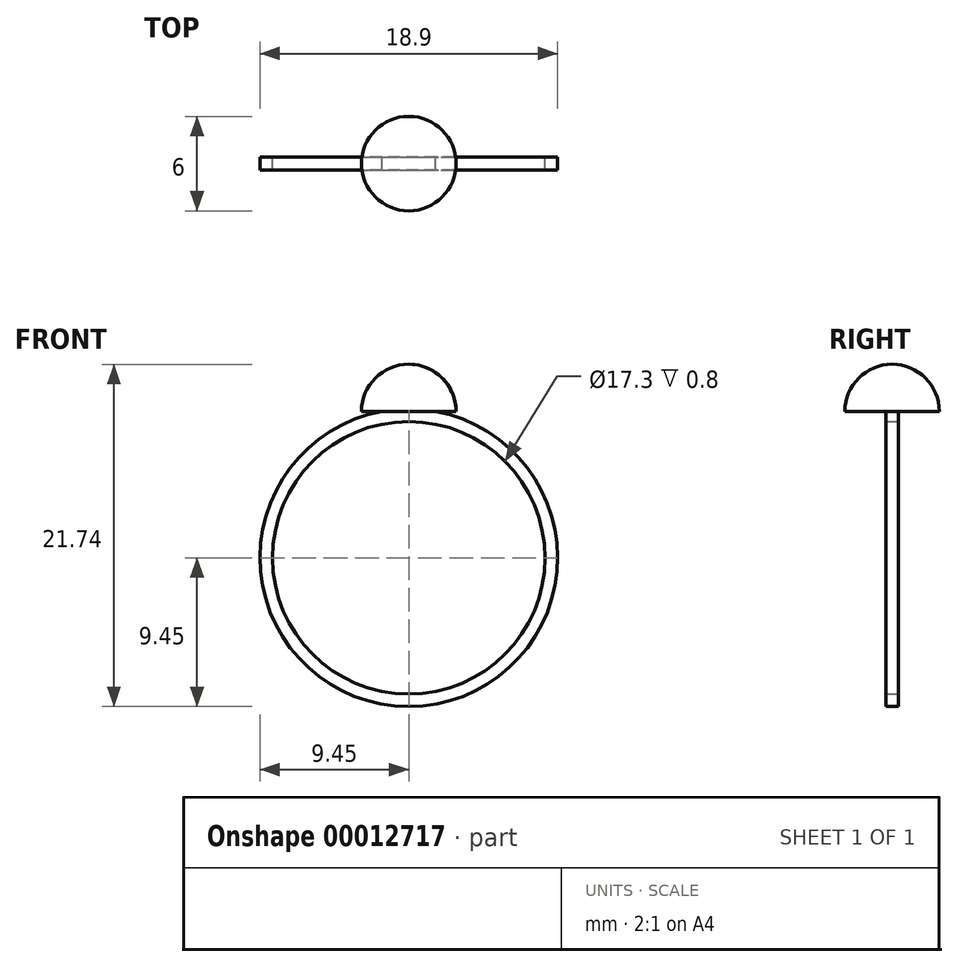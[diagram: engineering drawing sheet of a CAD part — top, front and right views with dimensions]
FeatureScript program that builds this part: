
annotation { "Feature Type Name" : "Feature", "Feature Type Description" : "" }
export const myFeature = defineFeature(function(context is Context, id is Id, definition is map)
    precondition{}
    {
        {
            var Q0;
            Q0=qCreatedBy(makeId("Front.planeOp"),FACE);
            var sketch = newSketch(context, id + "F0", { "sketchPlane" : qUnion([Q0])});
            skCircle(sketch, "E0", {"center": v(0, 0) * mm, "radius": 8.65 * mm});
            skCircle(sketch, "E1", {"center": v(0, 0) * mm, "radius": 9.45 * mm});
            skLineSegment(sketch, "E2", {"start": v(0, 0) * mm, "end": v(1.71, 9.3) * mm});
            skLineSegment(sketch, "E3", {"start": v(-1.71, 9.3) * mm, "end": v(0, 0) * mm});
            skLineSegment(sketch, "E4", {"start": v(-1.71, 9.3) * mm, "end": v(0, 9.3) * mm});
            skLineSegment(sketch, "E5", {"start": v(0, 9.3) * mm, "end": v(1.71, 9.3) * mm});
            skSolve(sketch);
        }
        {
            var Q0;
            {var subQ1=sQuery(id+"F0.wireOp",EDGE,"E0");var subQ5=sQuery(id+"F0.wireOp",EDGE,"E2");var subQ6=makeQuery(id+"F0.imprint","INTERSECT",VERTEX,{"derivedFrom":[subQ1,subQ5]});Q0=makeQuery(id+"F0.imprint","IMPRINT",FACE,{"disambiguationData":[TD([[makeQuery(id+"F0.imprint","IMPRINT",EDGE,{"disambiguationData":[TD([[subQ6,1.0]])],"derivedFrom":subQ1}),-1.0]])]});}
            var Q1;
            {var subQ1=sQuery(id+"F0.wireOp",EDGE,"E4");Q1=makeQuery(id+"F0.imprint","IMPRINT",FACE,{"disambiguationData":[TD([[makeQuery(id+"F0.imprint","IMPRINT",EDGE,{"derivedFrom":subQ1}),-1.0]])]});}
            extrude(context, id + "F1", {"entities" : qUnion([Q0, Q1]), "depth" : .4 * mm});
        }
        {
            var Q0;
            {var subQ1=sQuery(id+"F0.wireOp",EDGE,"E0");var subQ5=sQuery(id+"F0.wireOp",EDGE,"E2");var subQ6=makeQuery(id+"F0.imprint","INTERSECT",VERTEX,{"derivedFrom":[subQ1,subQ5]});Q0=makeQuery(id+"F0.imprint","IMPRINT",FACE,{"disambiguationData":[TD([[makeQuery(id+"F0.imprint","IMPRINT",EDGE,{"disambiguationData":[TD([[subQ6,1.0]])],"derivedFrom":subQ1}),-1.0]])]});}
            var Q1;
            {var subQ1=sQuery(id+"F0.wireOp",EDGE,"E4");Q1=makeQuery(id+"F0.imprint","IMPRINT",FACE,{"disambiguationData":[TD([[makeQuery(id+"F0.imprint","IMPRINT",EDGE,{"derivedFrom":subQ1}),-1.0]])]});}
            extrude(context, id + "F2", {"entities" : qUnion([Q0, Q1]), "operationType" : NewBodyOperationType.ADD, "oppositeDirection" : true, "depth" : .4 * mm});
        }
        {
            var Q0;
            {var subQ0=sQuery(id+"F0.wireOp",EDGE,"E4");var subQ1=sQuery(id+"F0.wireOp",EDGE,"E5");Q0=makeQuery(id+"F2.boolean.opBoolean","MERGE",FACE,{"derivedFrom":[makeQuery(id+"F1.opExtrude","SWEPT_FACE",FACE,{"disambiguationData":[OSD([subQ0,subQ1])]}),makeQuery(id+"F2.opExtrude","SWEPT_FACE",FACE,{"disambiguationData":[OSD([subQ0,subQ1])]})]});}
            var sketch = newSketch(context, id + "F3", { "sketchPlane" : qUnion([Q0])});
            skCircle(sketch, "E6", {"center": v(0, 0) * mm, "radius": 3 * mm});
            skSolve(sketch);
        }
        {
            var Q0;
            Q0 = qSketchRegion(id + "F3", true);
            extrude(context, id + "F4", {"entities" : qUnion([Q0]), "operationType" : NewBodyOperationType.ADD, "depth" : 3 * mm});
        }
        {
            var Q0;
            Q0=makeQuery(id+"F4.opExtrude","CAP_FACE",FACE,{"disambiguationData":[OSD([sQuery(id+"F3.wireOp",EDGE,"E6")])],"isStart":false});
            fillet(context, id + "F5", {"entities" : qUnion([Q0]), "radius" : 3 * mm, "tangentPropagation" : true, "allowEdgeOverflow" : false});
        }
    });
